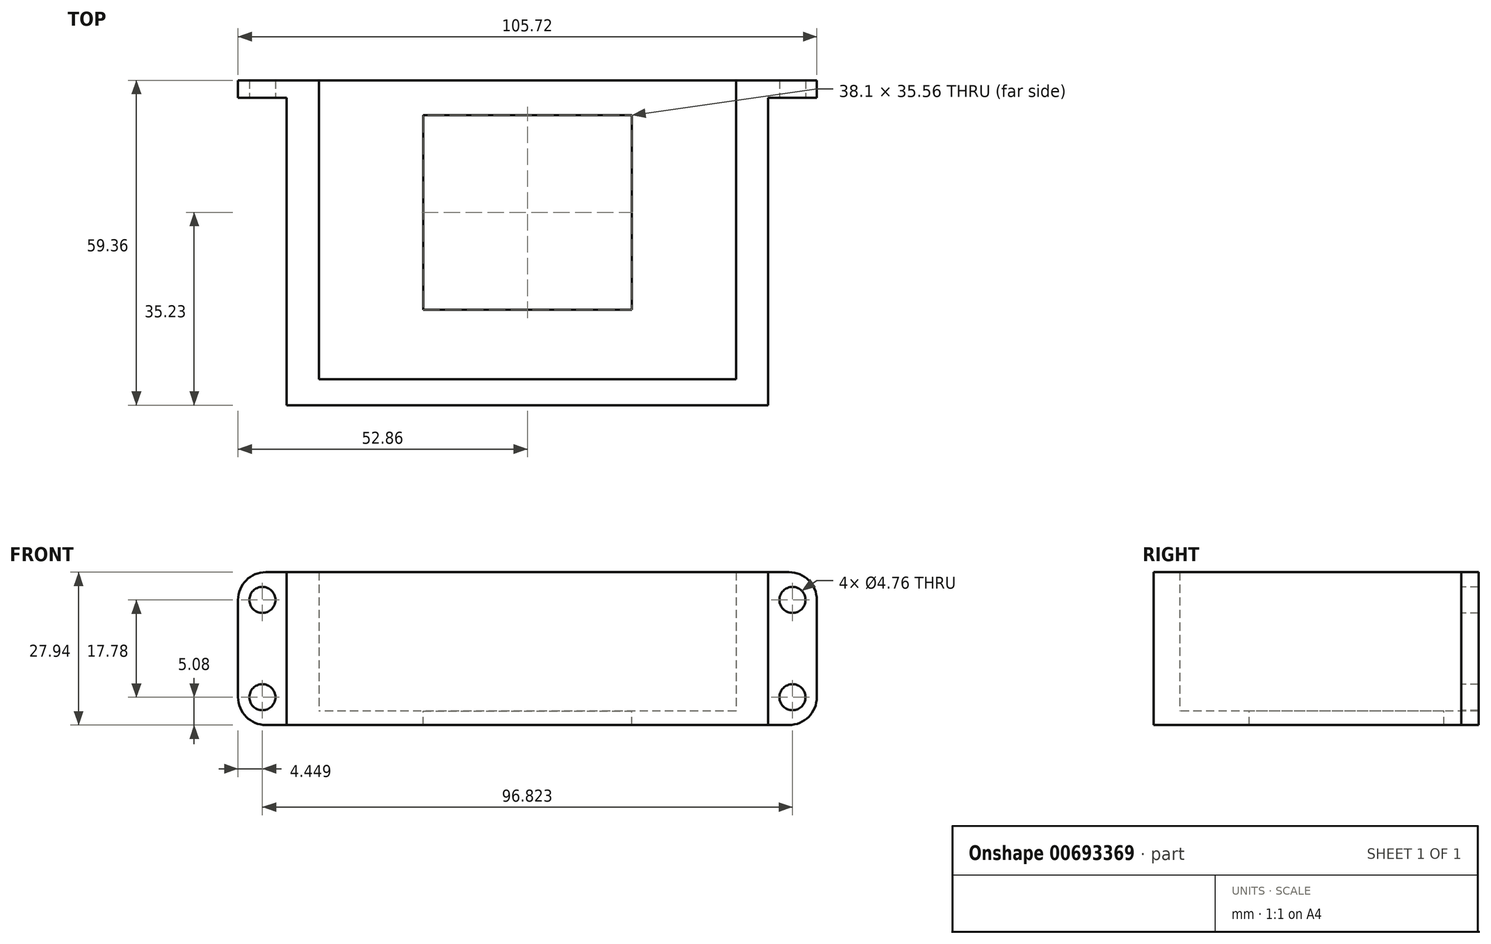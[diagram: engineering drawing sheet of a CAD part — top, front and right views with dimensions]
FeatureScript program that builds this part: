
annotation { "Feature Type Name" : "Feature", "Feature Type Description" : "" }
export const myFeature = defineFeature(function(context is Context, id is Id, definition is map)
    precondition{}
    {
        {
            var Q0;
            Q0=qCreatedBy(makeId("Top.planeOp"),FACE);
            var sketch = newSketch(context, id + "F0", { "sketchPlane" : qUnion([Q0])});
            skLineSegment(sketch, "E0.top", {"start": v(-38.1, -54.6) * mm, "end": v(38.1, -54.6) * mm});
            skLineSegment(sketch, "E0.left", {"start": v(-38.1, 0) * mm, "end": v(-38.1, -54.6) * mm});
            skLineSegment(sketch, "E0.right", {"start": v(38.1, 0) * mm, "end": v(38.1, -54.6) * mm});
            skPoint(sketch, "E0.middle", {"position": v(0, -27.3) * mm});
            skLineSegment(sketch, "E1.top", {"start": v(-43.97, -59.36) * mm, "end": v(43.97, -59.36) * mm});
            skLineSegment(sketch, "E1.left", {"start": v(-43.97, 0) * mm, "end": v(-43.97, -59.36) * mm});
            skLineSegment(sketch, "E1.right", {"start": v(43.97, 0) * mm, "end": v(43.97, -59.36) * mm});
            skLineSegment(sketch, "E2", {"start": v(-38.1, 0) * mm, "end": v(-43.97, 0) * mm});
            skLineSegment(sketch, "E3", {"start": v(38.1, 0) * mm, "end": v(43.97, 0) * mm});
            skPoint(sketch, "E1.bottom.start.orphan", {"position": v(-43.97, 4.75) * mm});
            skPoint(sketch, "E4.orphan", {"position": v(43.97, 4.75) * mm});
            skSolve(sketch);
        }
        {
            var Q0;
            Q0=makeQuery(id+"F0.imprint","IMPRINT",FACE,{"disambiguationData":[TD([[makeQuery(id+"F0.imprint","IMPRINT",EDGE,{"derivedFrom":sQuery(id+"F0.wireOp",EDGE,"E0.bottom")}),1.0]])]});
            var Q1;
            Q1=makeQuery(id+"F0.imprint","IMPRINT",FACE,{"disambiguationData":[TD([[makeQuery(id+"F0.imprint","IMPRINT",EDGE,{"derivedFrom":sQuery(id+"F0.wireOp",EDGE,"E0.top")}),-1.0]])]});
            extrude(context, id + "F1", {"entities" : qUnion([Q0, Q1]), "depth" : 25.4 * mm, "offsetDistance" : 25.4 * mm});
        }
        {
            var Q0;
            Q0=makeQuery(id+"F1.opExtrude","CAP_FACE",FACE,{"disambiguationData":[OSD([sQuery(id+"F0.wireOp",EDGE,"E0.top"),sQuery(id+"F0.wireOp",EDGE,"E0.left"),sQuery(id+"F0.wireOp",EDGE,"E0.right"),sQuery(id+"F0.wireOp",EDGE,"E1.top"),sQuery(id+"F0.wireOp",EDGE,"E1.left"),sQuery(id+"F0.wireOp",EDGE,"E1.right"),sQuery(id+"F0.wireOp",EDGE,"E2"),sQuery(id+"F0.wireOp",EDGE,"E3")])],"isStart":true});
            var sketch = newSketch(context, id + "F2", { "sketchPlane" : qUnion([Q0])});
            skLineSegment(sketch, "E5.bottom", {"start": v(-43.97, 59.36) * mm, "end": v(43.97, 59.36) * mm});
            skLineSegment(sketch, "E5.top", {"start": v(-43.97, 0) * mm, "end": v(43.97, 0) * mm});
            skLineSegment(sketch, "E5.left", {"start": v(-43.97, 59.36) * mm, "end": v(-43.97, 0) * mm});
            skLineSegment(sketch, "E5.right", {"start": v(43.97, 59.36) * mm, "end": v(43.97, 0) * mm});
            skSolve(sketch);
        }
        {
            var Q0;
            Q0 = qSketchRegion(id + "F2", true);
            extrude(context, id + "F3", {"entities" : qUnion([Q0]), "operationType" : NewBodyOperationType.ADD, "depth" : 2.54 * mm, "offsetDistance" : 25.4 * mm});
        }
        {
            var Q0;
            Q0=makeQuery(id+"F3.boolean.opBoolean","MERGE",FACE,{"derivedFrom":[makeQuery(id+"F1.opExtrude","SWEPT_FACE",FACE,{"disambiguationData":[OSD([sQuery(id+"F0.wireOp",EDGE,"E2")])]}),makeQuery(id+"F1.opExtrude","SWEPT_FACE",FACE,{"disambiguationData":[OSD([sQuery(id+"F0.wireOp",EDGE,"E3")])]}),makeQuery(id+"F3.opExtrude","SWEPT_FACE",FACE,{"disambiguationData":[OSD([sQuery(id+"F2.wireOp",EDGE,"E5.top")])]})]});
            var sketch = newSketch(context, id + "F4", { "sketchPlane" : qUnion([Q0])});
            skLineSegment(sketch, "E6.bottom", {"start": v(-43.97, 25.4) * mm, "end": v(-52.86, 25.4) * mm});
            skLineSegment(sketch, "E6.top", {"start": v(-43.97, -2.54) * mm, "end": v(-52.86, -2.54) * mm});
            skLineSegment(sketch, "E6.left", {"start": v(-43.97, 25.4) * mm, "end": v(-43.97, -2.54) * mm});
            skLineSegment(sketch, "E6.right", {"start": v(-52.86, 25.4) * mm, "end": v(-52.86, -2.54) * mm});
            skLineSegment(sketch, "E7.MirrorCS", {"start": v(52.86, 25.4) * mm, "end": v(52.86, -2.54) * mm});
            skLineSegment(sketch, "E8.MirrorCS", {"start": v(43.97, 25.4) * mm, "end": v(52.86, 25.4) * mm});
            skLineSegment(sketch, "E9.MirrorCS", {"start": v(43.97, -2.54) * mm, "end": v(52.86, -2.54) * mm});
            skLineSegment(sketch, "E10.MirrorCS", {"start": v(43.97, 25.4) * mm, "end": v(43.97, -2.54) * mm});
            skSolve(sketch);
        }
        {
            var Q0;
            Q0=makeQuery(id+"F4.imprint","IMPRINT",FACE,{"disambiguationData":[TD([[makeQuery(id+"F4.imprint","IMPRINT",EDGE,{"derivedFrom":sQuery(id+"F4.wireOp",EDGE,"E6.bottom")}),1.0]])]});
            var Q1;
            Q1=makeQuery(id+"F4.imprint","IMPRINT",FACE,{"disambiguationData":[TD([[makeQuery(id+"F4.imprint","IMPRINT",EDGE,{"derivedFrom":sQuery(id+"F4.wireOp",EDGE,"E7.MirrorCS")}),-1.0]])]});
            extrude(context, id + "F5", {"entities" : qUnion([Q0, Q1]), "operationType" : NewBodyOperationType.ADD, "oppositeDirection" : true, "depth" : 3.17 * mm, "offsetDistance" : 25.4 * mm});
        }
        {
            var Q0;
            Q0=makeQuery(id+"F3.opExtrude","CAP_FACE",FACE,{"disambiguationData":[OSD([sQuery(id+"F2.wireOp",EDGE,"E5.bottom"),sQuery(id+"F2.wireOp",EDGE,"E5.top"),sQuery(id+"F2.wireOp",EDGE,"E5.left"),sQuery(id+"F2.wireOp",EDGE,"E5.right")])],"isStart":true});
            var sketch = newSketch(context, id + "F6", { "sketchPlane" : qUnion([Q0])});
            skLineSegment(sketch, "E11.bottom", {"start": v(-19.05, -6.35) * mm, "end": v(0, -6.35) * mm});
            skLineSegment(sketch, "E11.top", {"start": v(-19.05, -41.9) * mm, "end": v(0, -41.9) * mm});
            skLineSegment(sketch, "E11.left", {"start": v(-19.05, -6.35) * mm, "end": v(-19.05, -41.9) * mm});
            skLineSegment(sketch, "E12.MirrorCS", {"start": v(19.05, -6.35) * mm, "end": v(0, -6.35) * mm});
            skLineSegment(sketch, "E13.MirrorCS", {"start": v(19.05, -6.35) * mm, "end": v(19.05, -41.9) * mm});
            skLineSegment(sketch, "E14.MirrorCS", {"start": v(19.05, -41.9) * mm, "end": v(0, -41.9) * mm});
            skSolve(sketch);
        }
        {
            var Q0;
            Q0=makeQuery(id+"F6.imprint","IMPRINT",FACE,{"disambiguationData":[TD([[makeQuery(id+"F6.imprint","IMPRINT",EDGE,{"derivedFrom":sQuery(id+"F6.wireOp",EDGE,"E11.bottom")}),-1.0]])]});
            extrude(context, id + "F7", {"entities" : qUnion([Q0]), "operationType" : NewBodyOperationType.REMOVE, "endBound" : BoundingType.THROUGH_ALL, "oppositeDirection" : true, "depth" : 25.4 * mm, "offsetDistance" : 25.4 * mm});
        }
        {
            var Q0;
            Q0=makeQuery(id+"F5.opExtrude","SWEPT_EDGE",EDGE,{"disambiguationData":[OSD([sQuery(id+"F4.wireOp",EDGE,"E6.bottom"),sQuery(id+"F4.wireOp",EDGE,"E6.right")])]});
            var Q1;
            Q1=makeQuery(id+"F5.opExtrude","SWEPT_EDGE",EDGE,{"disambiguationData":[OSD([sQuery(id+"F4.wireOp",EDGE,"E7.MirrorCS"),sQuery(id+"F4.wireOp",EDGE,"E8.MirrorCS")])]});
            var Q2;
            Q2=makeQuery(id+"F5.opExtrude","SWEPT_EDGE",EDGE,{"disambiguationData":[OSD([sQuery(id+"F4.wireOp",EDGE,"E7.MirrorCS"),sQuery(id+"F4.wireOp",EDGE,"E9.MirrorCS")])]});
            var Q3;
            Q3=makeQuery(id+"F5.opExtrude","SWEPT_EDGE",EDGE,{"disambiguationData":[OSD([sQuery(id+"F4.wireOp",EDGE,"E6.top"),sQuery(id+"F4.wireOp",EDGE,"E6.right")])]});
            fillet(context, id + "F8", {"entities" : qUnion([Q0, Q1, Q2, Q3]), "tangentPropagation" : true, "radius" : 5.08 * mm, "defaultsChanged" : false, "vertexSettings" : [], "allowEdgeOverflow" : false});
        }
        {
            var Q0;
            Q0=makeQuery(id+"F5.opExtrude","CAP_FACE",FACE,{"disambiguationData":[OSD([sQuery(id+"F4.wireOp",EDGE,"E6.bottom"),sQuery(id+"F4.wireOp",EDGE,"E6.top"),sQuery(id+"F4.wireOp",EDGE,"E6.left"),sQuery(id+"F4.wireOp",EDGE,"E6.right")])],"isStart":false});
            var sketch = newSketch(context, id + "F9", { "sketchPlane" : qUnion([Q0])});
            skLineSegment(sketch, "E15", {"start": v(52.86, 20.32) * mm, "end": v(43.97, 20.32) * mm, "construction": true});
            skCircle(sketch, "E16", {"center": v(48.41, 20.32) * mm, "radius": 2.38 * mm});
            skLineSegment(sketch, "E17", {"start": v(52.86, 11.43) * mm, "end": v(-60.9, 11.43) * mm, "construction": true});
            skCircle(sketch, "E18.MirrorC", {"center": v(48.41, 2.54) * mm, "radius": 2.38 * mm});
            skCircle(sketch, "E19.MirrorC", {"center": v(-48.41, 2.54) * mm, "radius": 2.38 * mm});
            skCircle(sketch, "E20.MirrorC", {"center": v(-48.41, 20.32) * mm, "radius": 2.38 * mm});
            skSolve(sketch);
        }
        {
            var Q0;
            Q0 = qSketchRegion(id + "F9", true);
            extrude(context, id + "F10", {"entities" : qUnion([Q0]), "operationType" : NewBodyOperationType.REMOVE, "endBound" : BoundingType.THROUGH_ALL, "oppositeDirection" : true, "depth" : 25.4 * mm, "offsetDistance" : 25.4 * mm});
        }
    });
